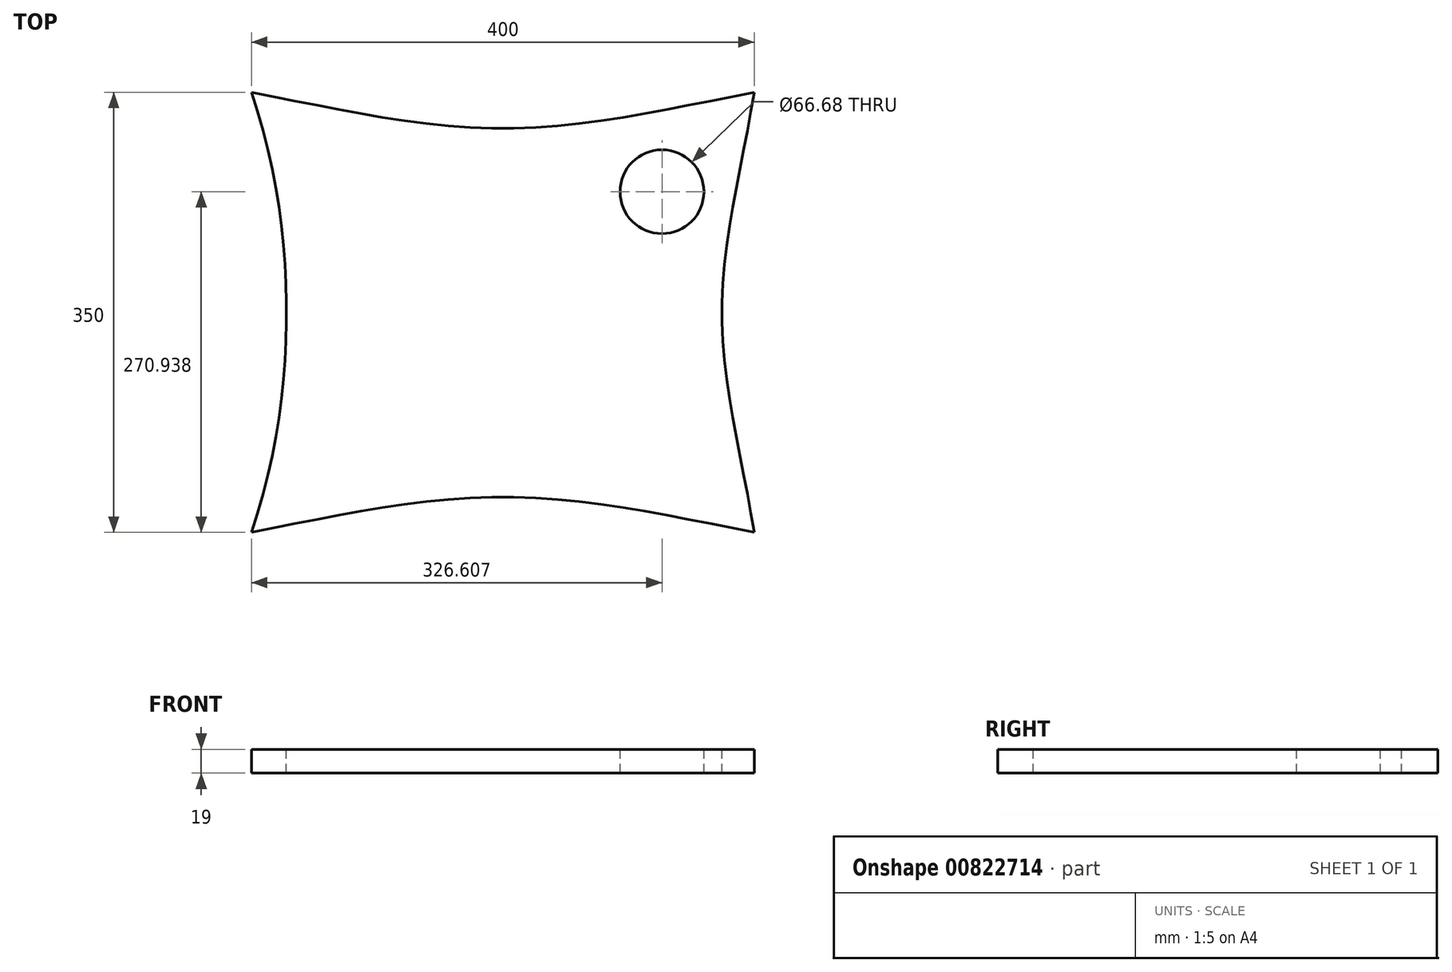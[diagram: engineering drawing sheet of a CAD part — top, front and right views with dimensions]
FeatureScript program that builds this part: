
annotation { "Feature Type Name" : "Feature", "Feature Type Description" : "" }
export const myFeature = defineFeature(function(context is Context, id is Id, definition is map)
    precondition{}
    {
        {
            var Q0;
            Q0=qCreatedBy(makeId("Top.planeOp"),FACE);
            var sketch = newSketch(context, id + "F0", { "sketchPlane" : qUnion([Q0])});
            skLineSegment(sketch, "E0.bottom", {"start": v(200, 175) * mm, "end": v(-200, 175) * mm});
            skLineSegment(sketch, "E0.top", {"start": v(200, -175) * mm, "end": v(-200, -175) * mm});
            skLineSegment(sketch, "E0.left", {"start": v(200, 175) * mm, "end": v(200, -175) * mm});
            skLineSegment(sketch, "E0.right", {"start": v(-200, 175) * mm, "end": v(-200, -175) * mm});
            skPoint(sketch, "E0.middle", {"position": v(0, 0) * mm});
            skSolve(sketch);
        }
        {
            var Q0;
            Q0 = qSketchRegion(id + "F0", true);
            extrude(context, id + "F1", {"entities" : qUnion([Q0]), "depth" : 19 * mm, "offsetDistance" : 25 * mm});
        }
        {
            var Q0;
            Q0=makeQuery(id+"F1.opExtrude","CAP_FACE",FACE,{"disambiguationData":[OSD([sQuery(id+"F0.wireOp",EDGE,"E0.bottom"),sQuery(id+"F0.wireOp",EDGE,"E0.top"),sQuery(id+"F0.wireOp",EDGE,"E0.left"),sQuery(id+"F0.wireOp",EDGE,"E0.right")])],"isStart":false});
            var sketch = newSketch(context, id + "F2", { "sketchPlane" : qUnion([Q0])});
            skFitSpline(sketch, "E1", {"points": [v(200, 175) * mm, v(0, 146.27) * mm, v(-200, 175) * mm], "startDerivative": vector(-400, -77.16) * mm, "endDerivative": vector(-400, 77.16) * mm});
            skFitSpline(sketch, "E2", {"points": [v(-200, 175) * mm, v(-172.22, 0) * mm, v(-200, -175) * mm], "startDerivative": vector(119.6, -350) * mm, "endDerivative": vector(-119.6, -350) * mm});
            skFitSpline(sketch, "E3", {"points": [v(-200, -175) * mm, v(0, -146.8) * mm, v(200, -175) * mm], "startDerivative": vector(400, 78.17) * mm, "endDerivative": vector(400, -78.17) * mm});
            skFitSpline(sketch, "E4", {"points": [v(200, 175) * mm, v(174.31, 0) * mm, v(200, -175) * mm], "startDerivative": vector(-57.3, -350) * mm, "endDerivative": vector(57.3, -350) * mm});
            skCircle(sketch, "E5", {"center": v(126.6, 95.94) * mm, "radius": 33.34 * mm});
            skSolve(sketch);
        }
        {
            var Q0;
            Q0=makeQuery(id+"F2.imprint","IMPRINT",FACE,{"disambiguationData":[TD([[makeQuery(id+"F2.imprint","IMPRINT",EDGE,{"derivedFrom":sQuery(id+"F2.wireOp",EDGE,"E1")}),-1.0]])]});
            extrude(context, id + "F3", {"entities" : qUnion([Q0]), "operationType" : NewBodyOperationType.REMOVE, "oppositeDirection" : true, "depth" : 25 * mm, "offsetDistance" : 25 * mm});
        }
        {
            var Q0;
            Q0=makeQuery(id+"F2.imprint","IMPRINT",FACE,{"disambiguationData":[TD([[makeQuery(id+"F2.imprint","IMPRINT",EDGE,{"derivedFrom":sQuery(id+"F2.wireOp",EDGE,"E2")}),-1.0]])]});
            extrude(context, id + "F4", {"entities" : qUnion([Q0]), "operationType" : NewBodyOperationType.REMOVE, "endBound" : BoundingType.THROUGH_ALL, "oppositeDirection" : true, "depth" : 25 * mm, "offsetDistance" : 25 * mm});
        }
        {
            var Q0;
            Q0=makeQuery(id+"F2.imprint","IMPRINT",FACE,{"disambiguationData":[TD([[makeQuery(id+"F2.imprint","IMPRINT",EDGE,{"derivedFrom":sQuery(id+"F2.wireOp",EDGE,"E3")}),-1.0]])]});
            extrude(context, id + "F5", {"entities" : qUnion([Q0]), "operationType" : NewBodyOperationType.REMOVE, "endBound" : BoundingType.THROUGH_ALL, "oppositeDirection" : true, "depth" : 25 * mm, "offsetDistance" : 25 * mm});
        }
        {
            var Q0;
            Q0=makeQuery(id+"F2.imprint","IMPRINT",FACE,{"disambiguationData":[TD([[makeQuery(id+"F2.imprint","IMPRINT",EDGE,{"derivedFrom":sQuery(id+"F2.wireOp",EDGE,"E4")}),1.0]])]});
            extrude(context, id + "F6", {"entities" : qUnion([Q0]), "operationType" : NewBodyOperationType.REMOVE, "endBound" : BoundingType.THROUGH_ALL, "oppositeDirection" : true, "depth" : 25 * mm, "offsetDistance" : 25 * mm});
        }
        {
            var Q0;
            Q0=makeQuery(id+"F2.imprint","IMPRINT",FACE,{"disambiguationData":[TD([[makeQuery(id+"F2.imprint","IMPRINT",EDGE,{"derivedFrom":sQuery(id+"F2.wireOp",EDGE,"E5")}),1.0]])]});
            extrude(context, id + "F7", {"entities" : qUnion([Q0]), "operationType" : NewBodyOperationType.REMOVE, "endBound" : BoundingType.THROUGH_ALL, "oppositeDirection" : true, "depth" : 25 * mm, "offsetDistance" : 25 * mm});
        }
    });
